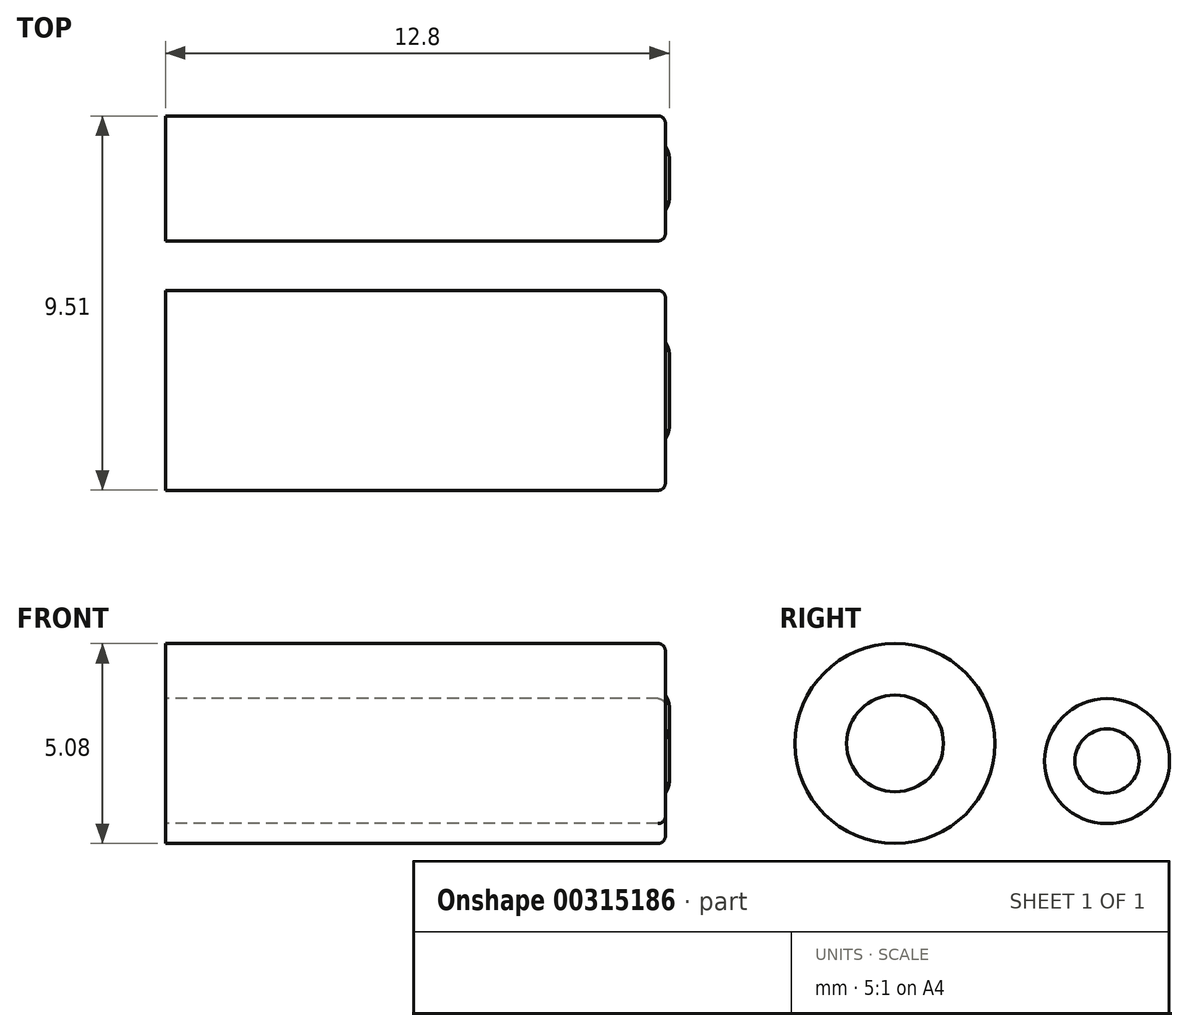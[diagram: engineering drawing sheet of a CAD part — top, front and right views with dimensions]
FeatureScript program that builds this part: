
annotation { "Feature Type Name" : "Feature", "Feature Type Description" : "" }
export const myFeature = defineFeature(function(context is Context, id is Id, definition is map)
    precondition{}
    {
        {
            var Q0;
            Q0=qCreatedBy(makeId("Right.planeOp"),FACE);
            var sketch = newSketch(context, id + "F0", { "sketchPlane" : qUnion([Q0])});
            skCircle(sketch, "E0", {"center": v(-44.8, 24.6) * mm, "radius": 2.54 * mm});
            skCircle(sketch, "E1", {"center": v(-39.42, 24.16) * mm, "radius": 1.59 * mm});
            skSolve(sketch);
        }
        {
            var Q0;
            Q0=makeQuery(id+"F0.imprint","IMPRINT",FACE,{"disambiguationData":[TD([[makeQuery(id+"F0.imprint","IMPRINT",EDGE,{"derivedFrom":sQuery(id+"F0.wireOp",EDGE,"E0")}),1.0]])]});
            var Q1;
            Q1=makeQuery(id+"F0.imprint","IMPRINT",FACE,{"disambiguationData":[TD([[makeQuery(id+"F0.imprint","IMPRINT",EDGE,{"derivedFrom":sQuery(id+"F0.wireOp",EDGE,"E1")}),1.0]])]});
            extrude(context, id + "F1", {"entities" : qUnion([Q0, Q1]), "depth" : 12.7 * mm});
        }
        {
            var Q0;
            Q0=makeQuery(id+"F1.opExtrude","CAP_EDGE",EDGE,{"disambiguationData":[OSD([sQuery(id+"F0.wireOp",EDGE,"E0")])],"isStart":false});
            var Q1;
            Q1=makeQuery(id+"F1.opExtrude","CAP_FACE",FACE,{"disambiguationData":[OSD([sQuery(id+"F0.wireOp",EDGE,"N4aTI13c-MIyW-n5gL-Bl1Z-qHBrhhcjHKI0")])],"isStart":false});
            var Q2;
            Q2=makeQuery(id+"F1.opExtrude","CAP_EDGE",EDGE,{"disambiguationData":[OSD([sQuery(id+"F0.wireOp",EDGE,"E1")])],"isStart":false});
            fillet(context, id + "F2", {"entities" : qUnion([Q0, Q1, Q2]), "radius" : 0.18 * mm, "tangentPropagation" : true, "allowEdgeOverflow" : false});
        }
        {
            var Q0;
            Q0=makeQuery(id+"F1.opExtrude","CAP_FACE",FACE,{"disambiguationData":[OSD([sQuery(id+"F0.wireOp",EDGE,"E0")])],"isStart":false});
            var sketch = newSketch(context, id + "F3", { "sketchPlane" : qUnion([Q0])});
            skCircle(sketch, "E2", {"center": v(-44.8, 24.6) * mm, "radius": 1.23 * mm});
            skSolve(sketch);
        }
        {
            var Q0;
            Q0=makeQuery(id+"F3.imprint","IMPRINT",FACE,{"disambiguationData":[TD([[makeQuery(id+"F3.imprint","IMPRINT",EDGE,{"derivedFrom":sQuery(id+"F3.wireOp",EDGE,"E2")}),1.0]])]});
            extrude(context, id + "F4", {"entities" : qUnion([Q0]), "depth" : 0.1 * mm});
        }
        {
            var Q0;
            Q0=makeQuery(id+"F1.opExtrude","CAP_FACE",FACE,{"disambiguationData":[OSD([sQuery(id+"F0.wireOp",EDGE,"E1")])],"isStart":false});
            var sketch = newSketch(context, id + "F5", { "sketchPlane" : qUnion([Q0])});
            skCircle(sketch, "E3", {"center": v(-39.42, 24.16) * mm, "radius": 0.82 * mm});
            skSolve(sketch);
        }
        {
            var Q0;
            Q0=makeQuery(id+"F5.imprint","IMPRINT",FACE,{"disambiguationData":[TD([[makeQuery(id+"F5.imprint","IMPRINT",EDGE,{"derivedFrom":sQuery(id+"F5.wireOp",EDGE,"E3")}),1.0]])]});
            extrude(context, id + "F6", {"entities" : qUnion([Q0]), "operationType" : NewBodyOperationType.ADD, "depth" : 0.1 * mm});
        }
        {
            var Q0;
            Q0=makeQuery(id+"F4.opExtrude","CAP_EDGE",EDGE,{"disambiguationData":[OSD([sQuery(id+"F3.wireOp",EDGE,"E2")])],"isStart":false});
            var Q1;
            Q1=makeQuery(id+"F6.opExtrude","CAP_EDGE",EDGE,{"disambiguationData":[OSD([sQuery(id+"F5.wireOp",EDGE,"E3")])],"isStart":false});
            fillet(context, id + "F7", {"entities" : qUnion([Q0, Q1]), "radius" : 0.5 * mm, "tangentPropagation" : true, "allowEdgeOverflow" : false});
        }
    });
